# Revit family: Rooftop_Screen-CityScapes-Envisor
name_source: partatom
category: Specialty Equipment
units: mm (PartAtom-declared; Revit-internal decimal feet)

## family parameters
Always vertical = Yes
Cut with Voids When Loaded = No
Part Type = Normal
Room Calculation Point = No
Round Connector Dimension = Use Diameter
Shared = No
Work Plane-Based = No

## types (15) — shared parameters
7.2 RIBBED VIZ = No
CAD Details = https://www.arcat.com
CornerFrameSystemDim = 4' - 0"
Default Elevation = 0' - 0"
Description = Adjustable Rooftop Mechanical Screen
Keynote = 10 82 13
Manufacturer = CityScapes
Model = Envisor
Panel_Length = 3' - 9"
Panel_Width = 0' - 2"
Product Page URL = https://www.arcat.com
SpacingLength = 6
Specification = https://www.arcat.com
System_Length = 22' - 6"
Type Comments = Envisor Screening Systems
URL = https://cityscapesinc.com

## per-type parameters (varying)
| type | 4.0 CORR HORT | 4.0 CORR VERT | 7.2 CORR VERT | 7.2 CORRUGATED | ABS_PANEL | BATTEN VIZ | FRAME MATERIAL | FRAME VIZ | FRAME WIDTH | LOUVRE VIZ | MATERIAL | Panel_Height | RIBBED VERT VIZ | RIBBED VIZ | SOLID PANEL VIZ | SpacingWidth | System_Width |
| 4.0 CORRUGATED HORIZONTAL SOLID | Yes | No | No | No | No | No | SHADOW GREY | Yes | 0' - 1 1/2" | No | SHADOW GREY | 4' - 0" | No | No | No | 6 | 22' - 6" |
| 7.2 RIB VERTICAL SOLID | No | No | Yes | No | No | No | SHADOW GREY | Yes | 0' - 1 1/2" | No | SHADOW GREY | 4' - 0" | No | No | No | 7 | 26' - 3" |
| 4.0 CORRUGATED VERTICAL SOLID | No | Yes | No | No | No | No | DARK BRONZE | Yes | 0' - 1 5/32" | No | DARK BRONZE | 3' - 0" | No | No | No | 7 | 26' - 3" |
| BATTEN VERT | No | No | No | No | Yes | Yes | ELECTRIC BLACK | No | 0' - 1 5/32" | No | ELECTRIC BLACK | 4' - 0" | No | No | No | 6 | 22' - 6" |
| ABS RIBBED VERT | No | No | No | No | Yes | No | FOREST GREEN | No | 0' - 1 5/32" | No | FOREST GREEN | 4' - 0" | Yes | No | No | 6 | 22' - 6" |
| VENTED LOUVER | No | No | No | No | No | No | SLATE GREY | Yes | 0' - 1 1/2" | Yes | SLATE GREY | 6' - 0" | No | No | No | 6 | 22' - 6" |
| ABS RIBBED HORIZONTAL | No | No | No | No | No | No | CITY BROWN TEXTURED | Yes | 0' - 1 1/2" | No | CITY BROWN TEXTURED | 4' - 0" | No | Yes | No | 6 | 22' - 6" |
| 7.2 RIBBED HORIZONTAL | No | No | No | Yes | Yes | No | MANSFORD BROWN | No | 0' - 1 1/2" | No | MANSFORD BROWN | 4' - 0" | No | No | No | 6 | 22' - 6" |
| PAN SOLID | No | No | No | No | No | No | SLATE BLUE | Yes | 0' - 1" | No | SLATE BLUE | 4' - 0" | No | No | Yes | 7 | 26' - 3" |
| FLAT PAN | No | No | No | No | Yes | No | PUTTY | No | 0' - 1 5/32" | No | PUTTY | 4' - 0" | No | No | Yes | 7 | 26' - 3" |
| CUSTOM | No | No | No | No | Yes | No | DARK BRONZE | No | 0' - 1 5/32" | No | DARK BRONZE | 4' - 0" | No | No | Yes | 7 | 26' - 3" |
| BRICK | No | No | No | No | Yes | No | TERRACOTTA | No | 0' - 1 1/2" | No | TERRACOTA BRICK | 4' - 0" | No | No | Yes | 7 | 26' - 3" |
| 7.2 RIB VERTICAL PERFORATED | No | No | Yes | No | No | No | OYSTER | Yes | 0' - 1 5/32" | No | OYSTER Perforated | 4' - 0" | No | No | No | 7 | 26' - 3" |
| PAN PERFORATED | No | No | No | No | No | No | OYSTER | Yes | 0' - 1 5/32" | No | OYSTER Perforated | 4' - 0" | No | No | Yes | 7 | 26' - 3" |
| 7.2 RIBBED HORIZONTAL PERFORATED | No | No | No | Yes | No | No | OYSTER | Yes | 0' - 1 1/4" | No | OYSTER Perforated | 4' - 0" | No | No | No | 6 | 22' - 6" |

## geometry (parser evidence)
native form markers: Sweep x34
no freeform markers — native parametric forms only
